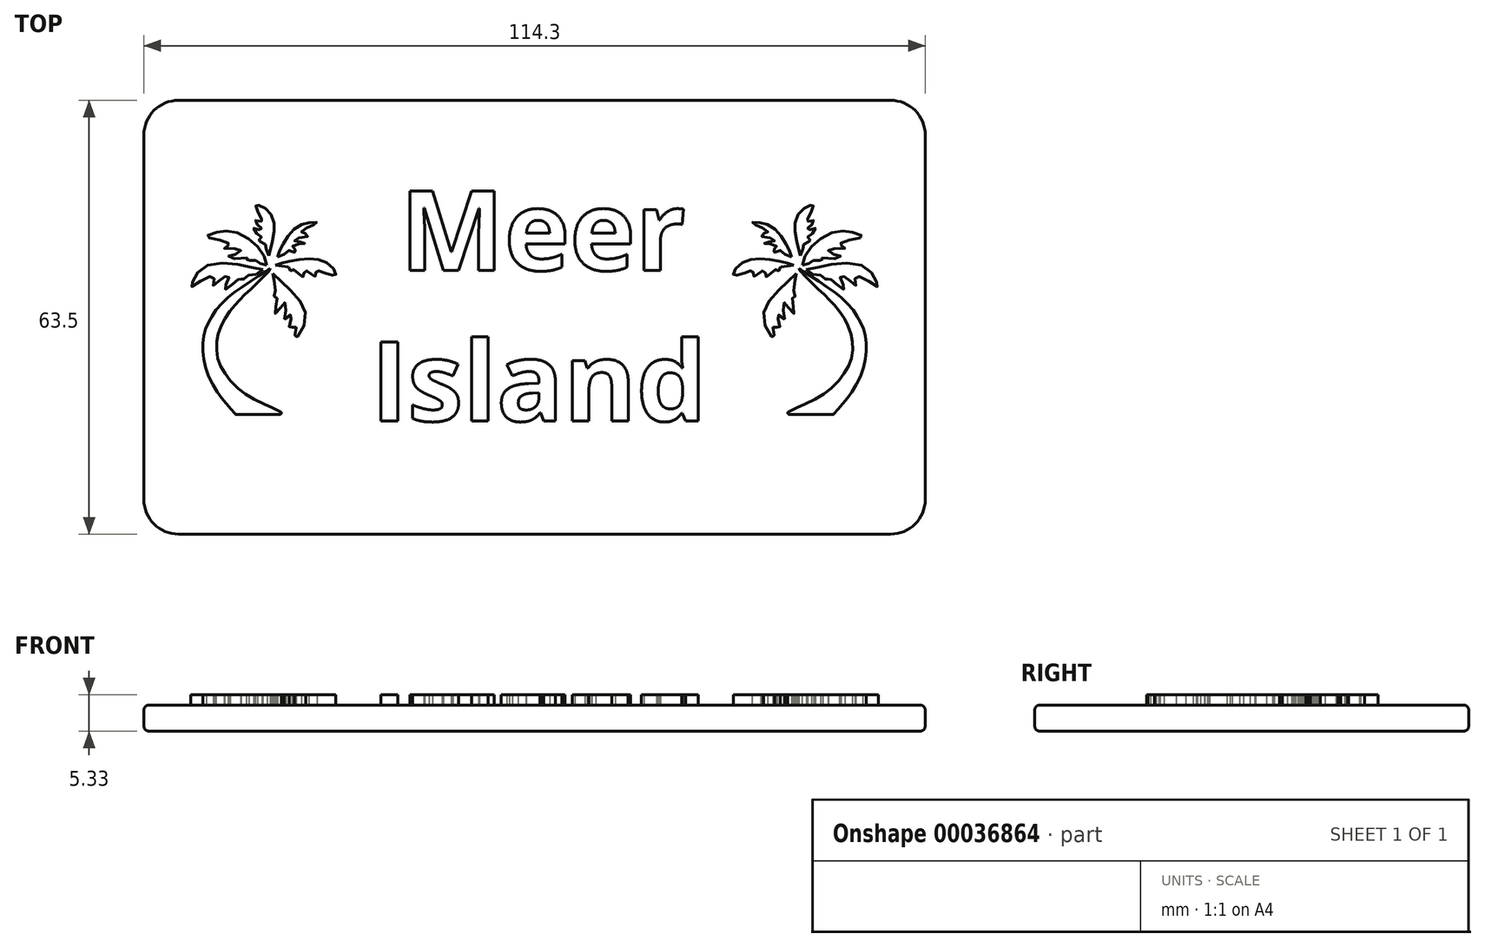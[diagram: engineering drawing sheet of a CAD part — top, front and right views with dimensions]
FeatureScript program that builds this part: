
annotation { "Feature Type Name" : "Feature", "Feature Type Description" : "" }
export const myFeature = defineFeature(function(context is Context, id is Id, definition is map)
    precondition{}
    {
        {
            var Q0;
            Q0=qCreatedBy(makeId("Top.planeOp"),FACE);
            var sketch = newSketch(context, id + "F0", { "sketchPlane" : qUnion([Q0])});
            skLineSegment(sketch, "E0.rect.bottom", {"start": v(57.15, -31.75) * mm, "end": v(-57.15, -31.75) * mm});
            skLineSegment(sketch, "E0.rect.top", {"start": v(57.15, 31.75) * mm, "end": v(-57.15, 31.75) * mm});
            skLineSegment(sketch, "E0.rect.left", {"start": v(57.15, -31.75) * mm, "end": v(57.15, 31.75) * mm});
            skLineSegment(sketch, "E0.rect.right", {"start": v(-57.15, -31.75) * mm, "end": v(-57.15, 31.75) * mm});
            skPoint(sketch, "E0.rect.middle", {"position": v(0, 0) * mm});
            skSolve(sketch);
        }
        {
            var Q0;
            Q0=makeQuery(id+"F0.imprint","IMPRINT",FACE,{"disambiguationData":[TD([[makeQuery(id+"F0.imprint","IMPRINT",EDGE,{"derivedFrom":sQuery(id+"F0.wireOp",EDGE,"E0.rect.bottom")}),-1.0]])]});
            extrude(context, id + "F1", {"entities" : qUnion([Q0]), "depth" : 3.8 * mm});
        }
        {
            var Q0;
            Q0=makeQuery(id+"F1.opExtrude","SWEPT_EDGE",EDGE,{"disambiguationData":[OSD([sQuery(id+"F0.wireOp",EDGE,"E0.rect.bottom"),sQuery(id+"F0.wireOp",EDGE,"E0.rect.right")])]});
            var Q1;
            Q1=makeQuery(id+"F1.opExtrude","SWEPT_EDGE",EDGE,{"disambiguationData":[OSD([sQuery(id+"F0.wireOp",EDGE,"E0.rect.bottom"),sQuery(id+"F0.wireOp",EDGE,"E0.rect.left")])]});
            var Q2;
            Q2=makeQuery(id+"F1.opExtrude","SWEPT_EDGE",EDGE,{"disambiguationData":[OSD([sQuery(id+"F0.wireOp",EDGE,"E0.rect.top"),sQuery(id+"F0.wireOp",EDGE,"E0.rect.left")])]});
            var Q3;
            Q3=makeQuery(id+"F1.opExtrude","SWEPT_EDGE",EDGE,{"disambiguationData":[OSD([sQuery(id+"F0.wireOp",EDGE,"E0.rect.top"),sQuery(id+"F0.wireOp",EDGE,"E0.rect.right")])]});
            fillet(context, id + "F2", {"entities" : qUnion([Q0, Q1, Q2, Q3]), "radius" : 5.08 * mm, "tangentPropagation" : true, "allowEdgeOverflow" : false});
        }
        {
            var Q0;
            Q0=makeQuery(id+"F1.opExtrude","CAP_FACE",FACE,{"disambiguationData":[OSD([sQuery(id+"F0.wireOp",EDGE,"E0.rect.bottom"),sQuery(id+"F0.wireOp",EDGE,"E0.rect.top"),sQuery(id+"F0.wireOp",EDGE,"E0.rect.left"),sQuery(id+"F0.wireOp",EDGE,"E0.rect.right")])],"isStart":false});
            var sketch = newSketch(context, id + "F3", { "sketchPlane" : qUnion([Q0])});
            skText(sketch, "E1", { "text": " Meer\nIsland", "fontName": "OpenSans-Bold.ttf"});
            const initialGuessF3  = {"E1": [-0.02393, 0.00688, 1, 0, 0.01168]};
            skSetInitialGuess(sketch, initialGuessF3);
            skSolve(sketch);
        }
        {
            var Q0;
            Q0 = qSketchRegion(id + "F3", true);
            extrude(context, id + "F4", {"entities" : qUnion([Q0]), "operationType" : NewBodyOperationType.ADD, "depth" : 1.52 * mm});
        }
        {
            var Q0;
            {var subQ0=sQuery(id+"F0.wireOp",EDGE,"E0.rect.bottom");var subQ1=sQuery(id+"F0.wireOp",EDGE,"E0.rect.top");var subQ2=sQuery(id+"F0.wireOp",EDGE,"E0.rect.left");var subQ3=sQuery(id+"F0.wireOp",EDGE,"E0.rect.right");Q0=makeQuery(id+"F4.boolean.opBoolean","SPLIT",FACE,{"disambiguationData":[TD([makeQuery(id+"F1.opExtrude","SWEPT_FACE",FACE,{"disambiguationData":[OSD([subQ0])]})])],"derivedFrom":makeQuery(id+"F1.opExtrude","CAP_FACE",FACE,{"disambiguationData":[OSD([subQ0,subQ1,subQ2,subQ3])],"isStart":false})});}
            var sketch = newSketch(context, id + "F5", { "sketchPlane" : qUnion([Q0])});
            skFitSpline(sketch, "E2", {"points": [v(-39.18, 7.61) * mm, v(-39.9, 7.77) * mm, v(-40.53, 8) * mm, v(-40.83, 8.34) * mm, v(-41.45, 8.36) * mm, v(-42.17, 8.22) * mm, v(-42.05, 8.42) * mm, v(-41.81, 8.74) * mm, v(-42.38, 8.6) * mm, v(-44.78, 8.8) * mm, v(-44.8, 8.92) * mm, v(-44.14, 9.08) * mm, v(-43.23, 9.51) * mm, v(-42.96, 9.81) * mm, v(-43.28, 9.98) * mm, v(-45.33, 10.07) * mm, v(-45.41, 10.18) * mm, v(-44.95, 10.44) * mm, v(-44.55, 10.69) * mm, v(-44.96, 10.92) * mm, v(-46.36, 11.38) * mm, v(-47.92, 11.71) * mm, v(-47.96, 11.9) * mm, v(-46.87, 12.32) * mm, v(-45.4, 12.6) * mm, v(-43.35, 12.34) * mm, v(-41.07, 10.85) * mm, v(-39.65, 9.12) * mm, v(-39.18, 7.61) * mm]});
            skFitSpline(sketch, "E3", {"points": [v(-38.85, 9) * mm, v(-39.15, 9.7) * mm, v(-39.26, 10.26) * mm, v(-39.33, 10.58) * mm, v(-39.77, 10.91) * mm, v(-40.33, 11.17) * mm, v(-40.5, 11.3) * mm, v(-40.32, 11.38) * mm, v(-40.06, 11.43) * mm, v(-39.9, 11.6) * mm, v(-40.15, 11.91) * mm, v(-40.6, 12.25) * mm, v(-41.09, 12.9) * mm, v(-41.05, 13.03) * mm, v(-40.67, 12.94) * mm, v(-40.2, 12.76) * mm, v(-39.93, 12.78) * mm, v(-39.98, 13.03) * mm, v(-40.37, 13.36) * mm, v(-40.72, 13.82) * mm, v(-40.86, 14.13) * mm, v(-40.7, 14.19) * mm, v(-40.18, 14.09) * mm, v(-39.82, 14.06) * mm, v(-39.8, 14.22) * mm, v(-40.05, 14.53) * mm, v(-40.4, 15.24) * mm, v(-40.6, 16) * mm, v(-40.84, 16.45) * mm, v(-40.65, 16.5) * mm, v(-40.06, 16.27) * mm, v(-39.32, 15.87) * mm, v(-38.58, 15.12) * mm, v(-38.14, 13.89) * mm, v(-38.08, 12.86) * mm, v(-38.29, 11.34) * mm, v(-38.64, 9.96) * mm, v(-38.8, 9.22) * mm, v(-38.85, 9) * mm]});
            skFitSpline(sketch, "E4", {"points": [v(-37.6, 8.82) * mm, v(-37.5, 9.39) * mm, v(-37.13, 10.02) * mm, v(-36.82, 10.62) * mm, v(-36.28, 11.6) * mm, v(-35.63, 12.41) * mm, v(-34.7, 13.24) * mm, v(-33.84, 13.69) * mm, v(-33.05, 13.85) * mm, v(-32.3, 13.85) * mm, v(-31.84, 13.89) * mm, v(-31.84, 13.73) * mm, v(-32.29, 13.54) * mm, v(-33.04, 13.24) * mm, v(-33.65, 12.9) * mm, v(-34.07, 12.56) * mm, v(-34.1, 12.39) * mm, v(-33.88, 12.32) * mm, v(-33.33, 12.16) * mm, v(-33.05, 11.93) * mm, v(-33.33, 11.8) * mm, v(-34.36, 11.65) * mm, v(-34.96, 11.39) * mm, v(-35.12, 11.19) * mm, v(-34.76, 11.07) * mm, v(-34.38, 11.04) * mm, v(-34.03, 10.95) * mm, v(-33.6, 10.82) * mm, v(-33.78, 10.75) * mm, v(-34.25, 10.74) * mm, v(-34.87, 10.64) * mm, v(-35.38, 10.39) * mm, v(-35.42, 10.21) * mm, v(-35.13, 10) * mm, v(-34.84, 9.44) * mm, v(-34.97, 9.41) * mm, v(-35.33, 9.58) * mm, v(-35.8, 9.8) * mm, v(-36.03, 9.73) * mm, v(-36.42, 9.35) * mm, v(-36.99, 9.08) * mm, v(-37.6, 8.82) * mm]});
            skFitSpline(sketch, "E5", {"points": [v(-37.9, 7.61) * mm, v(-37.28, 7.82) * mm, v(-36.66, 8.03) * mm, v(-35.45, 8.28) * mm, v(-33.94, 8.52) * mm, v(-32.37, 8.54) * mm, v(-31.27, 8.35) * mm, v(-30.14, 7.82) * mm, v(-29.33, 6.98) * mm, v(-29.09, 6.36) * mm, v(-29.09, 6.16) * mm, v(-29.25, 6.07) * mm, v(-29.76, 6.22) * mm, v(-30.74, 6.5) * mm, v(-31.37, 6.7) * mm, v(-31.74, 6.89) * mm, v(-31.89, 6.89) * mm, v(-31.95, 6.58) * mm, v(-32, 6.12) * mm, v(-32.1, 5.96) * mm, v(-32.4, 6.12) * mm, v(-32.72, 6.36) * mm, v(-33.14, 6.7) * mm, v(-33.36, 6.8) * mm, v(-33.6, 6.77) * mm, v(-33.74, 6.53) * mm, v(-33.76, 6.23) * mm, v(-33.83, 5.97) * mm, v(-33.96, 5.9) * mm, v(-34.33, 6.23) * mm, v(-34.8, 6.66) * mm, v(-35.27, 7) * mm, v(-35.47, 7.01) * mm, v(-35.57, 6.87) * mm, v(-35.74, 6.82) * mm, v(-35.86, 7.03) * mm, v(-36.02, 7.37) * mm, v(-36.63, 7.49) * mm, v(-37.57, 7.53) * mm, v(-37.9, 7.61) * mm]});
            skFitSpline(sketch, "E6", {"points": [v(-38.3, 6.41) * mm, v(-37.61, 5.82) * mm, v(-36.76, 4.97) * mm, v(-36.09, 4.33) * mm, v(-34.86, 3.07) * mm, v(-34.07, 2) * mm, v(-33.64, 1.04) * mm, v(-33.47, -0.18) * mm, v(-33.86, -1.5) * mm, v(-34.49, -2.53) * mm, v(-34.96, -3.14) * mm, v(-35.1, -3.08) * mm, v(-35.06, -2.82) * mm, v(-35.01, -2.47) * mm, v(-34.98, -2) * mm, v(-34.89, -1.47) * mm, v(-34.94, -1.22) * mm, v(-35.17, -1.23) * mm, v(-35.4, -1.42) * mm, v(-35.62, -1.62) * mm, v(-35.83, -1.75) * mm, v(-35.89, -1.67) * mm, v(-35.9, -1.36) * mm, v(-35.8, -0.96) * mm, v(-35.67, -0.44) * mm, v(-35.55, -0.05) * mm, v(-35.49, 0.25) * mm, v(-35.55, 0.43) * mm, v(-35.81, 0.23) * mm, v(-36.17, -0.07) * mm, v(-36.47, -0.27) * mm, v(-36.6, -0.2) * mm, v(-36.54, 0.24) * mm, v(-36.38, 1) * mm, v(-36.35, 1.6) * mm, v(-36.42, 2) * mm, v(-36.62, 2.18) * mm, v(-36.81, 1.85) * mm, v(-37.07, 1.46) * mm, v(-37.34, 1.08) * mm, v(-37.69, 0.71) * mm, v(-37.94, 0.55) * mm, v(-38.01, 0.58) * mm, v(-38, 0.9) * mm, v(-37.87, 1.48) * mm, v(-37.8, 1.97) * mm, v(-37.72, 2.62) * mm, v(-37.63, 3.06) * mm, v(-37.65, 3.26) * mm, v(-37.96, 3.13) * mm, v(-38.22, 3.04) * mm, v(-38.16, 3.31) * mm, v(-37.92, 3.8) * mm, v(-37.85, 4.41) * mm, v(-38.06, 5.3) * mm, v(-38.29, 5.97) * mm, v(-38.42, 6.26) * mm, v(-38.3, 6.41) * mm]});
            skFitSpline(sketch, "E7", {"points": [v(-39.75, 6.95) * mm, v(-40.35, 7) * mm, v(-41.58, 7.36) * mm, v(-43.03, 7.67) * mm, v(-44.67, 7.9) * mm, v(-46.4, 7.92) * mm, v(-47.95, 7.6) * mm, v(-48.9, 6.95) * mm, v(-49.56, 6.18) * mm, v(-49.94, 5.46) * mm, v(-50.2, 4.83) * mm, v(-50.28, 4.6) * mm, v(-50.25, 4.46) * mm, v(-50.07, 4.52) * mm, v(-49.45, 4.91) * mm, v(-48.92, 5.25) * mm, v(-48.06, 5.69) * mm, v(-47.4, 5.97) * mm, v(-46.96, 6.08) * mm, v(-46.85, 5.97) * mm, v(-46.87, 5.65) * mm, v(-46.94, 5.22) * mm, v(-47, 4.87) * mm, v(-46.99, 4.62) * mm, v(-46.87, 4.63) * mm, v(-46.62, 4.89) * mm, v(-46.23, 5.25) * mm, v(-45.79, 5.6) * mm, v(-45.43, 5.87) * mm, v(-45.16, 6.04) * mm, v(-44.93, 6.15) * mm, v(-44.76, 6.07) * mm, v(-44.72, 5.9) * mm, v(-44.84, 5.5) * mm, v(-45.04, 5) * mm, v(-45.2, 4.62) * mm, v(-45.32, 4.32) * mm, v(-45.36, 4.09) * mm, v(-45.26, 4.06) * mm, v(-44.89, 4.31) * mm, v(-44.38, 4.69) * mm, v(-44.05, 4.93) * mm, v(-43.78, 5.13) * mm, v(-43.42, 5.47) * mm, v(-43.25, 5.7) * mm, v(-43.15, 5.85) * mm, v(-43, 5.8) * mm, v(-42.93, 5.6) * mm, v(-42.9, 5.29) * mm, v(-42.79, 5.22) * mm, v(-42.68, 5.34) * mm, v(-42.5, 5.6) * mm, v(-42.34, 5.88) * mm, v(-42.17, 6.1) * mm, v(-41.83, 6.14) * mm, v(-41.41, 6.13) * mm, v(-41.04, 6.2) * mm, v(-40.46, 6.4) * mm, v(-40.13, 6.57) * mm, v(-39.75, 6.95) * mm]});
            skFitSpline(sketch, "E8", {"points": [v(-38.69, 7.18) * mm, v(-39.55, 6.58) * mm, v(-41.5, 5.32) * mm, v(-43.7, 3.78) * mm, v(-45.29, 2.48) * mm, v(-46.74, 0.83) * mm, v(-47.5, -0.38) * mm, v(-48.13, -1.76) * mm, v(-48.48, -3.16) * mm, v(-48.5, -4.89) * mm, v(-48.27, -6.76) * mm, v(-47.47, -9.04) * mm, v(-46.39, -11.01) * mm, v(-45.46, -12.23) * mm, v(-44.38, -13.42) * mm, v(-43.78, -14.21) * mm], "startDerivative": vector(-14.98, -10.98) * mm, "endDerivative": vector(10.69, -15.1) * mm});
            skLineSegment(sketch, "E9", {"start": v(-43.78, -14.21) * mm, "end": v(-36.65, -14.21) * mm});
            skFitSpline(sketch, "E10", {"points": [v(-36.65, -14.21) * mm, v(-37, -13.92) * mm, v(-37.9, -13.47) * mm, v(-39.02, -12.94) * mm, v(-40.48, -12.26) * mm, v(-41.97, -11.5) * mm, v(-42.9, -10.77) * mm, v(-44.1, -9.75) * mm, v(-45.07, -8.56) * mm, v(-45.53, -7.85) * mm, v(-46.07, -6.87) * mm, v(-46.38, -5.92) * mm, v(-46.5, -4.82) * mm, v(-46.53, -3.87) * mm, v(-46.38, -2.91) * mm, v(-46.2, -2.15) * mm, v(-45.7, -1.01) * mm, v(-45.31, -0.2) * mm, v(-44.66, 0.79) * mm, v(-44.05, 1.56) * mm, v(-43.58, 2.07) * mm, v(-43.16, 2.51) * mm, v(-42.52, 3.2) * mm, v(-41.9, 3.74) * mm, v(-41.2, 4.41) * mm, v(-40.37, 5.17) * mm, v(-39.5, 6.07) * mm, v(-38.93, 6.7) * mm, v(-38.68, 7) * mm, v(-38.63, 7.13) * mm, v(-38.69, 7.18) * mm], "startDerivative": vector(-12.84, 12.53) * mm, "endDerivative": vector(-7.76, 5.23) * mm});
            skLineSegment(sketch, "E11", {"start": v(0, 0) * mm, "end": v(0, 31.75) * mm, "construction": true});
            skFitSpline(sketch, "E12.MirrorC", {"points": [v(39.18, 7.61) * mm, v(39.9, 7.77) * mm, v(40.53, 8) * mm, v(40.83, 8.34) * mm, v(41.45, 8.36) * mm, v(42.17, 8.22) * mm, v(42.05, 8.42) * mm, v(41.81, 8.74) * mm, v(42.38, 8.6) * mm, v(44.78, 8.8) * mm, v(44.8, 8.92) * mm, v(44.14, 9.08) * mm, v(43.23, 9.51) * mm, v(42.96, 9.81) * mm, v(43.28, 9.98) * mm, v(45.33, 10.07) * mm, v(45.41, 10.18) * mm, v(44.95, 10.44) * mm, v(44.55, 10.69) * mm, v(44.96, 10.92) * mm, v(46.36, 11.38) * mm, v(47.92, 11.71) * mm, v(47.96, 11.9) * mm, v(46.87, 12.32) * mm, v(45.4, 12.6) * mm, v(43.35, 12.34) * mm, v(41.07, 10.85) * mm, v(39.65, 9.12) * mm, v(39.18, 7.61) * mm]});
            skFitSpline(sketch, "E13.MirrorC", {"points": [v(38.85, 9) * mm, v(39.15, 9.7) * mm, v(39.26, 10.26) * mm, v(39.33, 10.58) * mm, v(39.77, 10.91) * mm, v(40.33, 11.17) * mm, v(40.5, 11.3) * mm, v(40.32, 11.38) * mm, v(40.06, 11.43) * mm, v(39.9, 11.6) * mm, v(40.15, 11.91) * mm, v(40.6, 12.25) * mm, v(41.09, 12.9) * mm, v(41.05, 13.03) * mm, v(40.67, 12.94) * mm, v(40.2, 12.76) * mm, v(39.93, 12.78) * mm, v(39.98, 13.03) * mm, v(40.37, 13.36) * mm, v(40.72, 13.82) * mm, v(40.86, 14.13) * mm, v(40.7, 14.19) * mm, v(40.18, 14.09) * mm, v(39.82, 14.06) * mm, v(39.8, 14.22) * mm, v(40.05, 14.53) * mm, v(40.4, 15.24) * mm, v(40.6, 16) * mm, v(40.84, 16.45) * mm, v(40.65, 16.5) * mm, v(40.06, 16.27) * mm, v(39.32, 15.87) * mm, v(38.58, 15.12) * mm, v(38.14, 13.89) * mm, v(38.08, 12.86) * mm, v(38.29, 11.34) * mm, v(38.64, 9.96) * mm, v(38.8, 9.22) * mm, v(38.85, 9) * mm]});
            skFitSpline(sketch, "E14.MirrorC", {"points": [v(37.6, 8.82) * mm, v(37.5, 9.39) * mm, v(37.13, 10.02) * mm, v(36.82, 10.62) * mm, v(36.28, 11.6) * mm, v(35.63, 12.41) * mm, v(34.7, 13.24) * mm, v(33.84, 13.69) * mm, v(33.05, 13.85) * mm, v(32.3, 13.85) * mm, v(31.84, 13.89) * mm, v(31.84, 13.73) * mm, v(32.29, 13.54) * mm, v(33.04, 13.24) * mm, v(33.65, 12.9) * mm, v(34.07, 12.56) * mm, v(34.1, 12.39) * mm, v(33.88, 12.32) * mm, v(33.33, 12.16) * mm, v(33.05, 11.93) * mm, v(33.33, 11.8) * mm, v(34.36, 11.65) * mm, v(34.96, 11.39) * mm, v(35.12, 11.19) * mm, v(34.76, 11.07) * mm, v(34.38, 11.04) * mm, v(34.03, 10.95) * mm, v(33.6, 10.82) * mm, v(33.78, 10.75) * mm, v(34.25, 10.74) * mm, v(34.87, 10.64) * mm, v(35.38, 10.39) * mm, v(35.42, 10.21) * mm, v(35.13, 10) * mm, v(34.84, 9.44) * mm, v(34.97, 9.41) * mm, v(35.33, 9.58) * mm, v(35.8, 9.8) * mm, v(36.03, 9.73) * mm, v(36.42, 9.35) * mm, v(36.99, 9.08) * mm, v(37.6, 8.82) * mm]});
            skFitSpline(sketch, "E15.MirrorC", {"points": [v(37.9, 7.61) * mm, v(37.28, 7.82) * mm, v(36.66, 8.03) * mm, v(35.45, 8.28) * mm, v(33.94, 8.52) * mm, v(32.37, 8.54) * mm, v(31.27, 8.35) * mm, v(30.14, 7.82) * mm, v(29.33, 6.98) * mm, v(29.09, 6.36) * mm, v(29.09, 6.16) * mm, v(29.25, 6.07) * mm, v(29.76, 6.22) * mm, v(30.74, 6.5) * mm, v(31.37, 6.7) * mm, v(31.74, 6.89) * mm, v(31.89, 6.89) * mm, v(31.95, 6.58) * mm, v(32, 6.12) * mm, v(32.1, 5.96) * mm, v(32.4, 6.12) * mm, v(32.72, 6.36) * mm, v(33.14, 6.7) * mm, v(33.36, 6.8) * mm, v(33.6, 6.77) * mm, v(33.74, 6.53) * mm, v(33.76, 6.23) * mm, v(33.83, 5.97) * mm, v(33.96, 5.9) * mm, v(34.33, 6.23) * mm, v(34.8, 6.66) * mm, v(35.27, 7) * mm, v(35.47, 7.01) * mm, v(35.57, 6.87) * mm, v(35.74, 6.82) * mm, v(35.86, 7.03) * mm, v(36.02, 7.37) * mm, v(36.63, 7.49) * mm, v(37.57, 7.53) * mm, v(37.9, 7.61) * mm]});
            skFitSpline(sketch, "E16.MirrorC", {"points": [v(38.3, 6.41) * mm, v(37.61, 5.82) * mm, v(36.76, 4.97) * mm, v(36.09, 4.33) * mm, v(34.86, 3.07) * mm, v(34.07, 2) * mm, v(33.64, 1.04) * mm, v(33.47, -0.18) * mm, v(33.86, -1.5) * mm, v(34.49, -2.53) * mm, v(34.96, -3.14) * mm, v(35.1, -3.08) * mm, v(35.06, -2.82) * mm, v(35.01, -2.47) * mm, v(34.98, -2) * mm, v(34.89, -1.47) * mm, v(34.94, -1.22) * mm, v(35.17, -1.23) * mm, v(35.4, -1.42) * mm, v(35.62, -1.62) * mm, v(35.83, -1.75) * mm, v(35.89, -1.67) * mm, v(35.9, -1.36) * mm, v(35.8, -0.96) * mm, v(35.67, -0.44) * mm, v(35.55, -0.05) * mm, v(35.49, 0.25) * mm, v(35.55, 0.43) * mm, v(35.81, 0.23) * mm, v(36.17, -0.07) * mm, v(36.47, -0.27) * mm, v(36.6, -0.2) * mm, v(36.54, 0.24) * mm, v(36.38, 1) * mm, v(36.35, 1.6) * mm, v(36.42, 2) * mm, v(36.62, 2.18) * mm, v(36.81, 1.85) * mm, v(37.07, 1.46) * mm, v(37.34, 1.08) * mm, v(37.69, 0.71) * mm, v(37.94, 0.55) * mm, v(38.01, 0.58) * mm, v(38, 0.9) * mm, v(37.87, 1.48) * mm, v(37.8, 1.97) * mm, v(37.72, 2.62) * mm, v(37.63, 3.06) * mm, v(37.65, 3.26) * mm, v(37.96, 3.13) * mm, v(38.22, 3.04) * mm, v(38.16, 3.31) * mm, v(37.92, 3.8) * mm, v(37.85, 4.41) * mm, v(38.06, 5.3) * mm, v(38.29, 5.97) * mm, v(38.42, 6.26) * mm, v(38.3, 6.41) * mm]});
            skFitSpline(sketch, "E17.MirrorC", {"points": [v(39.75, 6.95) * mm, v(40.35, 7) * mm, v(41.58, 7.36) * mm, v(43.03, 7.67) * mm, v(44.67, 7.9) * mm, v(46.4, 7.92) * mm, v(47.95, 7.6) * mm, v(48.9, 6.95) * mm, v(49.56, 6.18) * mm, v(49.94, 5.46) * mm, v(50.2, 4.83) * mm, v(50.28, 4.6) * mm, v(50.25, 4.46) * mm, v(50.07, 4.52) * mm, v(49.45, 4.91) * mm, v(48.92, 5.25) * mm, v(48.06, 5.69) * mm, v(47.4, 5.97) * mm, v(46.96, 6.08) * mm, v(46.85, 5.97) * mm, v(46.87, 5.65) * mm, v(46.94, 5.22) * mm, v(47, 4.87) * mm, v(46.99, 4.62) * mm, v(46.87, 4.63) * mm, v(46.62, 4.89) * mm, v(46.23, 5.25) * mm, v(45.79, 5.6) * mm, v(45.43, 5.87) * mm, v(45.16, 6.04) * mm, v(44.93, 6.15) * mm, v(44.76, 6.07) * mm, v(44.72, 5.9) * mm, v(44.84, 5.5) * mm, v(45.04, 5) * mm, v(45.2, 4.62) * mm, v(45.32, 4.32) * mm, v(45.36, 4.09) * mm, v(45.26, 4.06) * mm, v(44.89, 4.31) * mm, v(44.38, 4.69) * mm, v(44.05, 4.93) * mm, v(43.78, 5.13) * mm, v(43.42, 5.47) * mm, v(43.25, 5.7) * mm, v(43.15, 5.85) * mm, v(43, 5.8) * mm, v(42.93, 5.6) * mm, v(42.9, 5.29) * mm, v(42.79, 5.22) * mm, v(42.68, 5.34) * mm, v(42.5, 5.6) * mm, v(42.34, 5.88) * mm, v(42.17, 6.1) * mm, v(41.83, 6.14) * mm, v(41.41, 6.13) * mm, v(41.04, 6.2) * mm, v(40.46, 6.4) * mm, v(40.13, 6.57) * mm, v(39.75, 6.95) * mm]});
            skFitSpline(sketch, "E18.MirrorCS", {"points": [v(38.69, 7.18) * mm, v(39.55, 6.58) * mm, v(41.5, 5.32) * mm, v(43.7, 3.78) * mm, v(45.29, 2.48) * mm, v(46.74, 0.83) * mm, v(47.5, -0.38) * mm, v(48.13, -1.76) * mm, v(48.48, -3.16) * mm, v(48.5, -4.89) * mm, v(48.27, -6.76) * mm, v(47.47, -9.04) * mm, v(46.39, -11.01) * mm, v(45.46, -12.23) * mm, v(44.38, -13.42) * mm, v(43.78, -14.21) * mm], "startDerivative": vector(14.98, -10.98) * mm, "endDerivative": vector(-10.69, -15.1) * mm});
            skFitSpline(sketch, "E19.MirrorCS", {"points": [v(36.65, -14.21) * mm, v(37, -13.92) * mm, v(37.9, -13.47) * mm, v(39.02, -12.94) * mm, v(40.48, -12.26) * mm, v(41.97, -11.5) * mm, v(42.9, -10.77) * mm, v(44.1, -9.75) * mm, v(45.07, -8.56) * mm, v(45.53, -7.85) * mm, v(46.07, -6.87) * mm, v(46.38, -5.92) * mm, v(46.5, -4.82) * mm, v(46.53, -3.87) * mm, v(46.38, -2.91) * mm, v(46.2, -2.15) * mm, v(45.7, -1.01) * mm, v(45.31, -0.2) * mm, v(44.66, 0.79) * mm, v(44.05, 1.56) * mm, v(43.58, 2.07) * mm, v(43.16, 2.51) * mm, v(42.52, 3.2) * mm, v(41.9, 3.74) * mm, v(41.2, 4.41) * mm, v(40.37, 5.17) * mm, v(39.5, 6.07) * mm, v(38.93, 6.7) * mm, v(38.68, 7) * mm, v(38.63, 7.13) * mm, v(38.69, 7.18) * mm], "startDerivative": vector(12.84, 12.53) * mm, "endDerivative": vector(7.76, 5.23) * mm});
            skLineSegment(sketch, "E20.MirrorCS", {"start": v(43.78, -14.21) * mm, "end": v(36.65, -14.21) * mm});
            skSolve(sketch);
        }
        {
            var Q0;
            Q0=makeQuery(id+"F5.imprint","IMPRINT",FACE,{"disambiguationData":[TD([[makeQuery(id+"F5.imprint","IMPRINT",EDGE,{"derivedFrom":sQuery(id+"F5.wireOp",EDGE,"E8")}),1.0]])]});
            var Q1;
            Q1=makeQuery(id+"F5.imprint","IMPRINT",FACE,{"disambiguationData":[TD([[makeQuery(id+"F5.imprint","IMPRINT",EDGE,{"derivedFrom":sQuery(id+"F5.wireOp",EDGE,"E7")}),1.0]])]});
            var Q2;
            Q2=makeQuery(id+"F5.imprint","IMPRINT",FACE,{"disambiguationData":[TD([[makeQuery(id+"F5.imprint","IMPRINT",EDGE,{"derivedFrom":sQuery(id+"F5.wireOp",EDGE,"E2")}),-1.0]])]});
            var Q3;
            Q3=makeQuery(id+"F5.imprint","IMPRINT",FACE,{"disambiguationData":[TD([[makeQuery(id+"F5.imprint","IMPRINT",EDGE,{"derivedFrom":sQuery(id+"F5.wireOp",EDGE,"E3")}),-1.0]])]});
            var Q4;
            Q4=makeQuery(id+"F5.imprint","IMPRINT",FACE,{"disambiguationData":[TD([[makeQuery(id+"F5.imprint","IMPRINT",EDGE,{"derivedFrom":sQuery(id+"F5.wireOp",EDGE,"E4")}),-1.0]])]});
            var Q5;
            Q5=makeQuery(id+"F5.imprint","IMPRINT",FACE,{"disambiguationData":[TD([[makeQuery(id+"F5.imprint","IMPRINT",EDGE,{"derivedFrom":sQuery(id+"F5.wireOp",EDGE,"E5")}),-1.0]])]});
            var Q6;
            Q6=makeQuery(id+"F5.imprint","IMPRINT",FACE,{"disambiguationData":[TD([[makeQuery(id+"F5.imprint","IMPRINT",EDGE,{"derivedFrom":sQuery(id+"F5.wireOp",EDGE,"E6")}),-1.0]])]});
            var Q7;
            Q7=makeQuery(id+"F5.imprint","IMPRINT",FACE,{"disambiguationData":[TD([[makeQuery(id+"F5.imprint","IMPRINT",EDGE,{"derivedFrom":sQuery(id+"F5.wireOp",EDGE,"E15.MirrorC")}),1.0]])]});
            var Q8;
            Q8=makeQuery(id+"F5.imprint","IMPRINT",FACE,{"disambiguationData":[TD([[makeQuery(id+"F5.imprint","IMPRINT",EDGE,{"derivedFrom":sQuery(id+"F5.wireOp",EDGE,"E14.MirrorC")}),1.0]])]});
            var Q9;
            Q9=makeQuery(id+"F5.imprint","IMPRINT",FACE,{"disambiguationData":[TD([[makeQuery(id+"F5.imprint","IMPRINT",EDGE,{"derivedFrom":sQuery(id+"F5.wireOp",EDGE,"E13.MirrorC")}),1.0]])]});
            var Q10;
            Q10=makeQuery(id+"F5.imprint","IMPRINT",FACE,{"disambiguationData":[TD([[makeQuery(id+"F5.imprint","IMPRINT",EDGE,{"derivedFrom":sQuery(id+"F5.wireOp",EDGE,"E12.MirrorC")}),1.0]])]});
            var Q11;
            Q11=makeQuery(id+"F5.imprint","IMPRINT",FACE,{"disambiguationData":[TD([[makeQuery(id+"F5.imprint","IMPRINT",EDGE,{"derivedFrom":sQuery(id+"F5.wireOp",EDGE,"E17.MirrorC")}),-1.0]])]});
            var Q12;
            Q12=makeQuery(id+"F5.imprint","IMPRINT",FACE,{"disambiguationData":[TD([[makeQuery(id+"F5.imprint","IMPRINT",EDGE,{"derivedFrom":sQuery(id+"F5.wireOp",EDGE,"E16.MirrorC")}),1.0]])]});
            var Q13;
            Q13=makeQuery(id+"F5.imprint","IMPRINT",FACE,{"disambiguationData":[TD([[makeQuery(id+"F5.imprint","IMPRINT",EDGE,{"derivedFrom":sQuery(id+"F5.wireOp",EDGE,"E18.MirrorCS")}),-1.0]])]});
            extrude(context, id + "F6", {"entities" : qUnion([Q0, Q1, Q2, Q3, Q4, Q5, Q6, Q7, Q8, Q9, Q10, Q11, Q12, Q13]), "operationType" : NewBodyOperationType.ADD, "depth" : 1.52 * mm});
        }
        {
            var Q0;
            Q0=makeQuery(id+"F6.opExtrude","SWEPT_EDGE",EDGE,{"disambiguationData":[OSD([sQuery(id+"F5.wireOp",EDGE,"E9"),sQuery(id+"F5.wireOp",EDGE,"E10")])]});
            var Q1;
            Q1=makeQuery(id+"F6.opExtrude","SWEPT_EDGE",EDGE,{"disambiguationData":[OSD([sQuery(id+"F5.wireOp",EDGE,"E8"),sQuery(id+"F5.wireOp",EDGE,"E9")])]});
            var Q2;
            Q2=makeQuery(id+"F6.opExtrude","SWEPT_EDGE",EDGE,{"disambiguationData":[OSD([sQuery(id+"F5.wireOp",EDGE,"E19.MirrorCS"),sQuery(id+"F5.wireOp",EDGE,"E20.MirrorCS")])]});
            var Q3;
            Q3=makeQuery(id+"F6.opExtrude","SWEPT_EDGE",EDGE,{"disambiguationData":[OSD([sQuery(id+"F5.wireOp",EDGE,"E18.MirrorCS"),sQuery(id+"F5.wireOp",EDGE,"E20.MirrorCS")])]});
            fillet(context, id + "F7", {"entities" : qUnion([Q0, Q1, Q2, Q3]), "radius" : 0.2 * mm, "tangentPropagation" : true, "allowEdgeOverflow" : false});
        }
        {
            var Q0;
            Q0=makeQuery(id+"F1.opExtrude","CAP_EDGE",EDGE,{"disambiguationData":[OSD([sQuery(id+"F0.wireOp",EDGE,"E0.rect.bottom")])],"isStart":false});
            var Q1;
            Q1=makeQuery(id+"F1.opExtrude","CAP_EDGE",EDGE,{"disambiguationData":[OSD([sQuery(id+"F0.wireOp",EDGE,"E0.rect.bottom")])],"isStart":true});
            fillet(context, id + "F8", {"entities" : qUnion([Q0, Q1]), "radius" : 0.76 * mm, "tangentPropagation" : true, "allowEdgeOverflow" : false});
        }
    });
